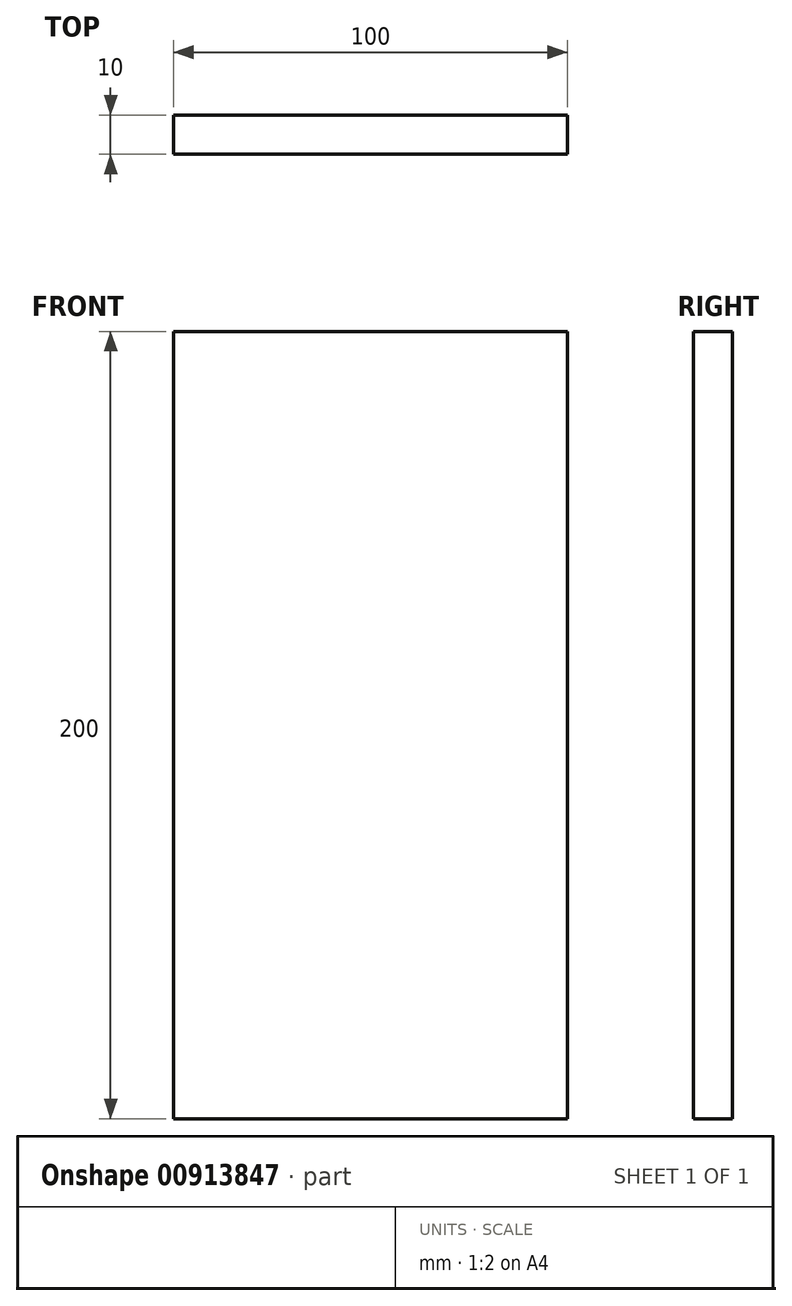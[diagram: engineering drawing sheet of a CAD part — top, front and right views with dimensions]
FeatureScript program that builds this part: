
annotation { "Feature Type Name" : "Feature", "Feature Type Description" : "" }
export const myFeature = defineFeature(function(context is Context, id is Id, definition is map)
    precondition{}
    {
        {
            var Q0;
            Q0=qCreatedBy(makeId("Front.planeOp"),FACE);
            var sketch = newSketch(context, id + "F0", { "sketchPlane" : qUnion([Q0])});
            skLineSegment(sketch, "E0.bottom", {"start": v(0, 0) * mm, "end": v(100, 0) * mm});
            skLineSegment(sketch, "E0.top", {"start": v(0, 200) * mm, "end": v(100, 200) * mm});
            skLineSegment(sketch, "E0.left", {"start": v(0, 0) * mm, "end": v(0, 200) * mm});
            skLineSegment(sketch, "E0.right", {"start": v(100, 0) * mm, "end": v(100, 200) * mm});
            skSolve(sketch);
        }
        {
            var Q0;
            Q0=qSketchRegion(id+"F0",true);
            extrude(context, id + "F1", {"entities" : qUnion([Q0]), "depth" : 10 * mm, "offsetDistance" : 25 * mm});
        }
    });
